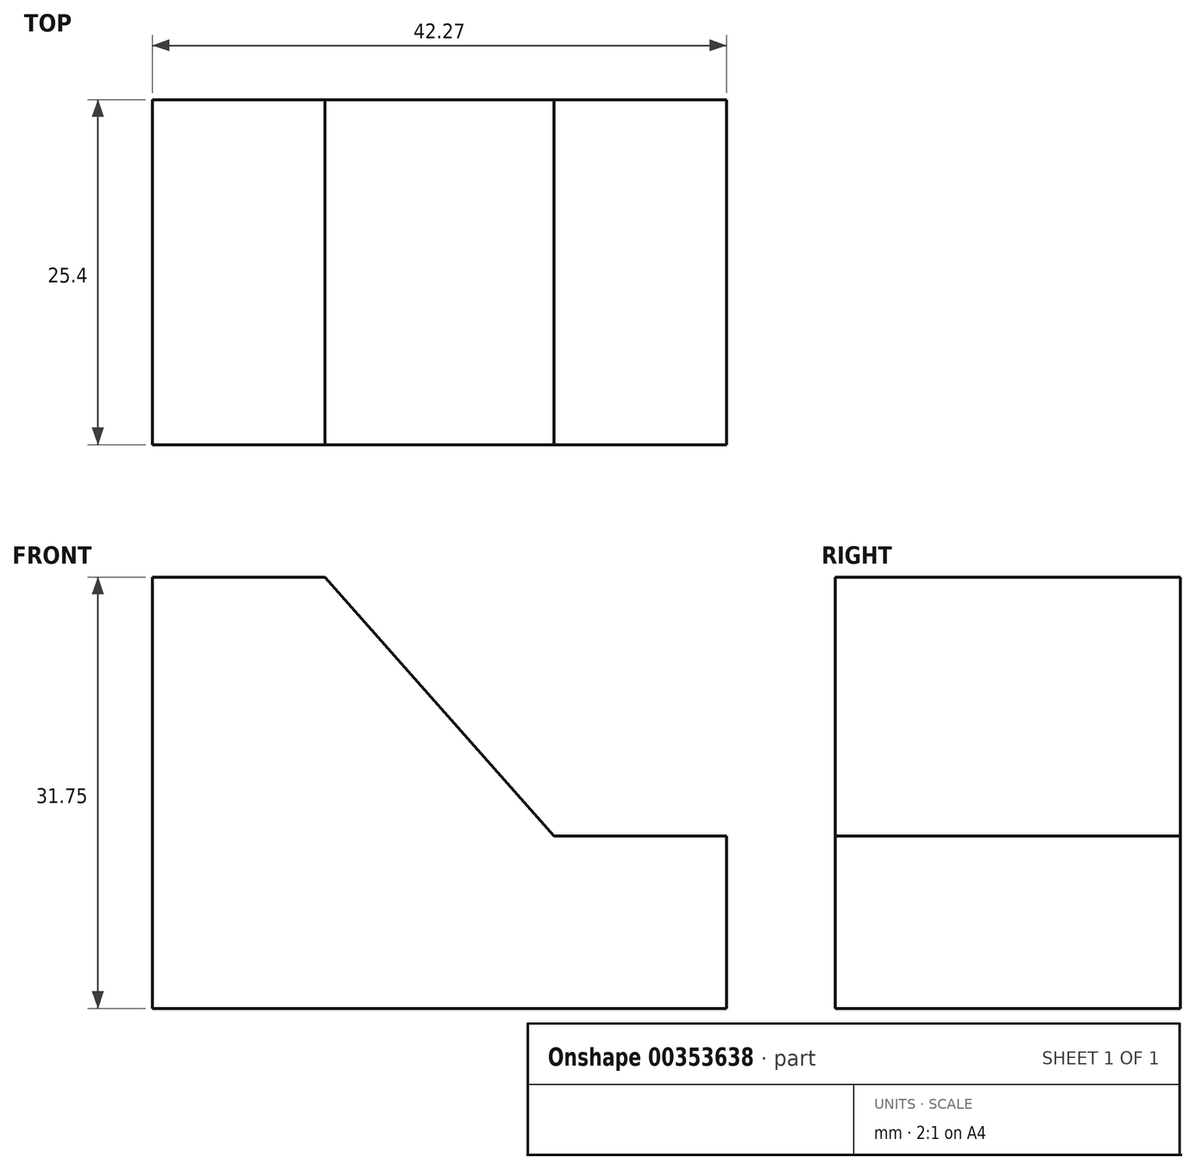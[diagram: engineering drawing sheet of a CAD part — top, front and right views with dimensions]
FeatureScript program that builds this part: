
annotation { "Feature Type Name" : "Feature", "Feature Type Description" : "" }
export const myFeature = defineFeature(function(context is Context, id is Id, definition is map)
    precondition{}
    {
        {
            var Q0;
            Q0=qCreatedBy(makeId("Front.planeOp"),FACE);
            var sketch = newSketch(context, id + "F0", { "sketchPlane" : qUnion([Q0])});
            skLineSegment(sketch, "E0", {"start": v(0, 0) * mm, "end": v(0, 31.75) * mm});
            skLineSegment(sketch, "E1", {"start": v(0, 31.75) * mm, "end": v(12.7, 31.75) * mm});
            skLineSegment(sketch, "E2", {"start": v(12.7, 31.75) * mm, "end": v(29.57, 12.7) * mm});
            skLineSegment(sketch, "E3", {"start": v(29.57, 12.7) * mm, "end": v(42.27, 12.7) * mm});
            skLineSegment(sketch, "E4", {"start": v(42.27, 12.7) * mm, "end": v(42.27, 0) * mm});
            skLineSegment(sketch, "E5", {"start": v(42.27, 0) * mm, "end": v(0, 0) * mm});
            skSolve(sketch);
        }
        {
            var Q0;
            Q0=makeQuery(id+"F0.imprint","IMPRINT",FACE,{"disambiguationData":[TD([[makeQuery(id+"F0.imprint","IMPRINT",EDGE,{"derivedFrom":sQuery(id+"F0.wireOp",EDGE,"E0")}),-1.0]])]});
            extrude(context, id + "F1", {"entities" : qUnion([Q0]), "depth" : 25.4 * mm});
        }
    });
